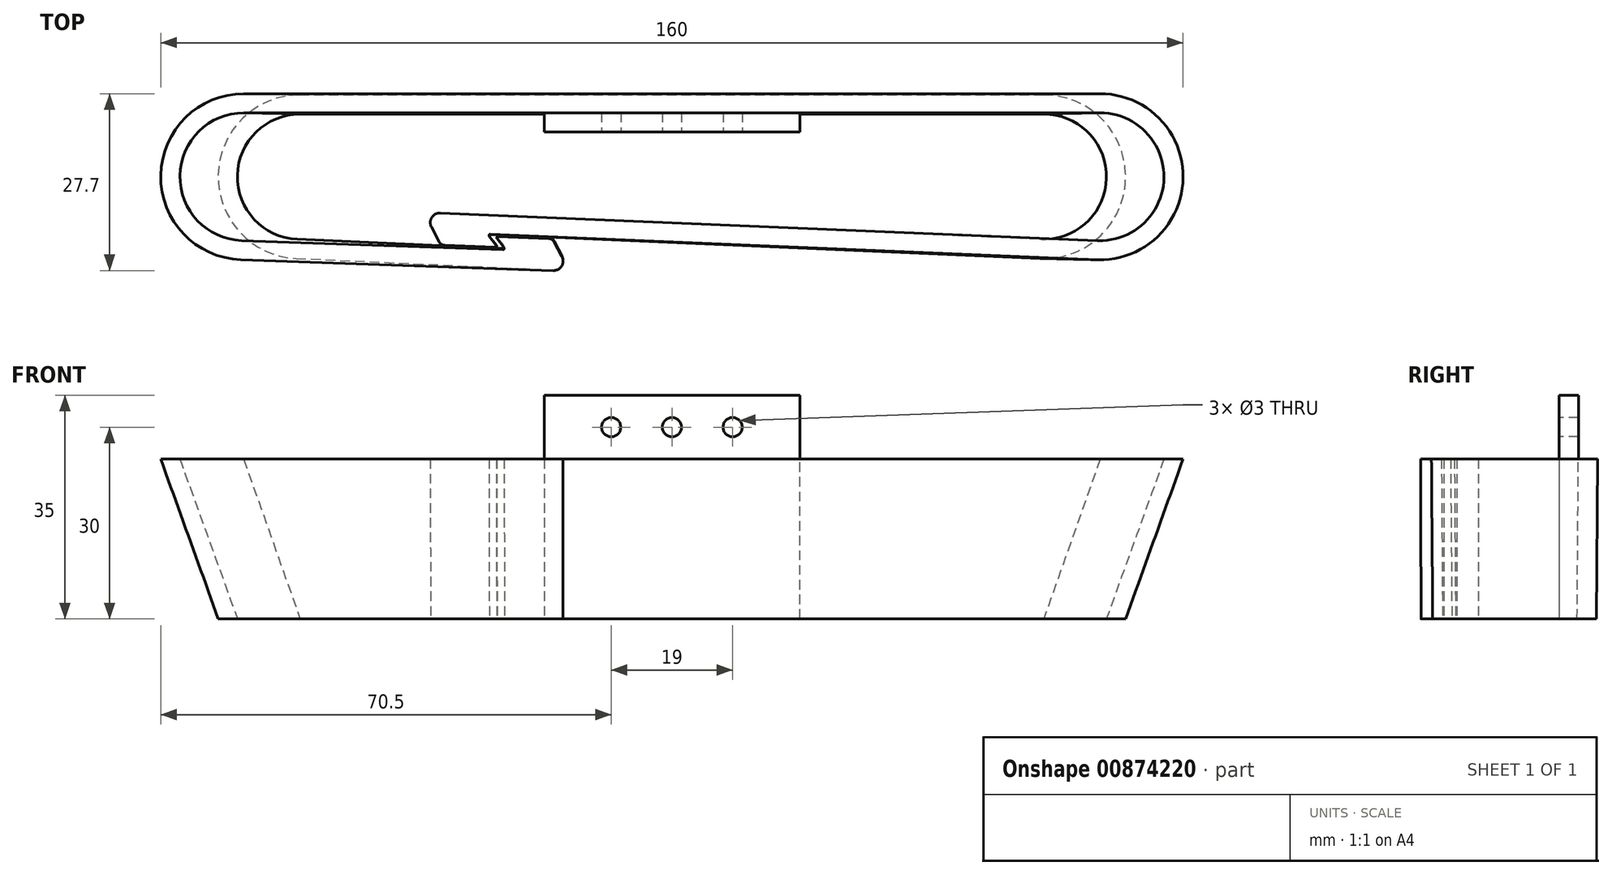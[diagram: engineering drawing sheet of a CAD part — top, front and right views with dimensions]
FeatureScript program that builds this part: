
annotation { "Feature Type Name" : "Feature", "Feature Type Description" : "" }
export const myFeature = defineFeature(function(context is Context, id is Id, definition is map)
    precondition{}
    {
        {
            var Q0;
            Q0=qCreatedBy(makeId("Top.planeOp"),FACE);
            var sketch = newSketch(context, id + "F0", { "sketchPlane" : qUnion([Q0])});
            skPoint(sketch, "E0.middle", {"position": v(0, 0) * mm});
            skArc(sketch, "E1", {"start": v(66.46, -12.99) * mm, "mid": v(80, -0.27) * mm, "end": v(67, 13) * mm});
            skLineSegment(sketch, "E2", {"start": v(67, 13) * mm, "end": v(-67, 13) * mm});
            skArc(sketch, "E3", {"start": v(-67, 13) * mm, "mid": v(-80, 0.23) * mm, "end": v(-67.45, -13) * mm});
            skLineSegment(sketch, "E4", {"start": v(66.46, -12.99) * mm, "end": v(-28.42, -9.01) * mm});
            skLineSegment(sketch, "E5", {"start": v(0, 13) * mm, "end": v(0, -10.2) * mm, "construction": true});
            skLineSegment(sketch, "E6", {"start": v(-16, 0) * mm, "end": v(-16, -14.79) * mm, "construction": true});
            skLineSegment(sketch, "E7", {"start": v(-67.45, -13) * mm, "end": v(-18.6, -14.7) * mm});
            skLineSegment(sketch, "E8", {"start": v(-67, 0) * mm, "end": v(-16, 0) * mm, "construction": true});
            skLineSegment(sketch, "E9.0", {"start": v(66.58, -10) * mm, "end": v(-36.26, -5.68) * mm});
            skLineSegment(sketch, "E9.1", {"start": v(-67.35, -10) * mm, "end": v(-26.46, -11.42) * mm});
            skArc(sketch, "E9.2", {"start": v(-67, 10) * mm, "mid": v(-77, 0.17) * mm, "end": v(-67.35, -10) * mm});
            skLineSegment(sketch, "E9.3", {"start": v(67, 10) * mm, "end": v(-67, 10) * mm});
            skArc(sketch, "E9.4", {"start": v(66.58, -10) * mm, "mid": v(77, -0.2) * mm, "end": v(67, 10) * mm});
            skLineSegment(sketch, "E10", {"start": v(-27.2, -9.4) * mm, "end": v(-19.29, -9.67) * mm});
            skLineSegment(sketch, "E11", {"start": v(-18.44, -10.2) * mm, "end": v(-17.22, -12.5) * mm});
            skPoint(sketch, "E12.visualSharp", {"position": v(-16, -14.79) * mm});
            skArc(sketch, "E12.filletArc", {"start": v(-18.6, -14.7) * mm, "mid": v(-17.27, -14) * mm, "end": v(-17.22, -12.5) * mm});
            skPoint(sketch, "E13.visualSharp", {"position": v(-18.71, -9.7) * mm});
            skArc(sketch, "E13.filletArc", {"start": v(-18.44, -10.2) * mm, "mid": v(-18.8, -9.82) * mm, "end": v(-19.29, -9.67) * mm});
            skPoint(sketch, "E14.visualSharp", {"position": v(-27.2, -9.4) * mm});
            skArc(sketch, "E14.filletArc", {"start": v(-27.2, -9.4) * mm, "mid": v(-27.4, -9.5) * mm, "end": v(-27.37, -9.72) * mm});
            skLineSegment(sketch, "E15", {"start": v(0, 0) * mm, "end": v(67, 0) * mm, "construction": true});
            skLineSegment(sketch, "E16", {"start": v(-28.59, -9.33) * mm, "end": v(-27.52, -10.72) * mm});
            skLineSegment(sketch, "E17", {"start": v(-27.69, -11.04) * mm, "end": v(-35.6, -10.71) * mm});
            skLineSegment(sketch, "E18", {"start": v(-36.45, -10.18) * mm, "end": v(-37.65, -7.87) * mm});
            skPoint(sketch, "E19.visualSharp", {"position": v(-36.18, -10.69) * mm});
            skArc(sketch, "E19.filletArc", {"start": v(-36.45, -10.18) * mm, "mid": v(-36.1, -10.56) * mm, "end": v(-35.6, -10.71) * mm});
            skPoint(sketch, "E20.visualSharp", {"position": v(-38.85, -5.57) * mm});
            skArc(sketch, "E20.filletArc", {"start": v(-36.26, -5.68) * mm, "mid": v(-37.59, -6.38) * mm, "end": v(-37.65, -7.87) * mm});
            skArc(sketch, "E21.filletArc", {"start": v(-27.69, -11.04) * mm, "mid": v(-27.5, -10.94) * mm, "end": v(-27.52, -10.72) * mm});
            skPoint(sketch, "E22.visualSharp", {"position": v(-28.85, -9) * mm});
            skArc(sketch, "E22.filletArc", {"start": v(-28.42, -9.01) * mm, "mid": v(-28.6, -9.12) * mm, "end": v(-28.59, -9.33) * mm});
            skLineSegment(sketch, "E23", {"start": v(-16, 0) * mm, "end": v(0, 0) * mm, "construction": true});
            skArc(sketch, "E24", {"start": v(-26.46, -11.42) * mm, "mid": v(-26.27, -11.31) * mm, "end": v(-26.3, -11.1) * mm});
            skLineSegment(sketch, "E25", {"start": v(-27.37, -9.72) * mm, "end": v(-26.3, -11.1) * mm});
            skLineSegment(sketch, "E26", {"start": v(-27.37, -9.47) * mm, "end": v(-27.37, -10.97) * mm, "construction": true});
            skLineSegment(sketch, "E27", {"start": v(-27.52, -10.72) * mm, "end": v(-27.52, -9.22) * mm, "construction": true});
            skSolve(sketch);
        }
        {
            var Q0;
            Q0=qCreatedBy(makeId("Top.planeOp"),FACE);
            cPlane(context, id + "F1", {"entities" : qUnion([Q0]), "cplaneType" : CPlaneType.OFFSET, "offset" : 25 * mm, "oppositeDirection" : true, "width" : 150 * mm, "height" : 150 * mm});
        }
        {
            var Q0;
            Q0=qCreatedBy(id+"F1.planeOp",FACE);
            var sketch = newSketch(context, id + "F2", { "sketchPlane" : qUnion([Q0])});
            skPoint(sketch, "E28.middle", {"position": v(0, 0) * mm});
            skArc(sketch, "E29", {"start": v(57.64, -12.79) * mm, "mid": v(71, -0.28) * mm, "end": v(58.2, 12.8) * mm});
            skLineSegment(sketch, "E30", {"start": v(58.2, 12.8) * mm, "end": v(-58.2, 12.8) * mm});
            skArc(sketch, "E31", {"start": v(-58.2, 12.8) * mm, "mid": v(-71, 0.3) * mm, "end": v(-58.78, -12.79) * mm});
            skLineSegment(sketch, "E32", {"start": v(57.64, -12.79) * mm, "end": v(-28.37, -9.03) * mm});
            skLineSegment(sketch, "E33", {"start": v(0, 12.8) * mm, "end": v(0, -10.27) * mm, "construction": true});
            skLineSegment(sketch, "E34", {"start": v(-16, 0) * mm, "end": v(-16, -14.73) * mm, "construction": true});
            skLineSegment(sketch, "E35", {"start": v(-58.78, -12.79) * mm, "end": v(-18.6, -14.61) * mm});
            skLineSegment(sketch, "E36", {"start": v(-58.2, 0) * mm, "end": v(-16, 0) * mm, "construction": true});
            skLineSegment(sketch, "E37.0", {"start": v(57.77, -9.8) * mm, "end": v(-36.2, -5.69) * mm});
            skLineSegment(sketch, "E37.1", {"start": v(-58.64, -9.79) * mm, "end": v(-26.42, -11.25) * mm});
            skArc(sketch, "E37.2", {"start": v(-58.2, 9.8) * mm, "mid": v(-68, 0.22) * mm, "end": v(-58.64, -9.79) * mm});
            skLineSegment(sketch, "E37.3", {"start": v(58.2, 9.8) * mm, "end": v(-58.2, 9.8) * mm});
            skArc(sketch, "E37.4", {"start": v(57.77, -9.8) * mm, "mid": v(68, -0.21) * mm, "end": v(58.2, 9.8) * mm});
            skLineSegment(sketch, "E38", {"start": v(-27.15, -9.22) * mm, "end": v(-19.23, -9.58) * mm});
            skLineSegment(sketch, "E39", {"start": v(-18.4, -10.12) * mm, "end": v(-17.2, -12.42) * mm});
            skPoint(sketch, "E40.visualSharp", {"position": v(-16, -14.73) * mm});
            skArc(sketch, "E40.filletArc", {"start": v(-18.6, -14.61) * mm, "mid": v(-17.26, -13.92) * mm, "end": v(-17.2, -12.42) * mm});
            skPoint(sketch, "E41.visualSharp", {"position": v(-18.66, -9.6) * mm});
            skArc(sketch, "E41.filletArc", {"start": v(-18.4, -10.12) * mm, "mid": v(-18.74, -9.73) * mm, "end": v(-19.23, -9.58) * mm});
            skPoint(sketch, "E42.visualSharp", {"position": v(-27.15, -9.22) * mm});
            skArc(sketch, "E42.filletArc", {"start": v(-27.15, -9.22) * mm, "mid": v(-27.33, -9.33) * mm, "end": v(-27.32, -9.54) * mm});
            skLineSegment(sketch, "E43", {"start": v(0, 0) * mm, "end": v(58.2, 0) * mm, "construction": true});
            skLineSegment(sketch, "E44", {"start": v(-28.53, -9.35) * mm, "end": v(-27.47, -10.74) * mm});
            skLineSegment(sketch, "E45", {"start": v(-27.63, -11.07) * mm, "end": v(-35.55, -10.72) * mm});
            skLineSegment(sketch, "E46", {"start": v(-36.4, -10.18) * mm, "end": v(-37.6, -7.88) * mm});
            skPoint(sketch, "E47.visualSharp", {"position": v(-36.13, -10.7) * mm});
            skArc(sketch, "E47.filletArc", {"start": v(-36.4, -10.18) * mm, "mid": v(-36.04, -10.57) * mm, "end": v(-35.55, -10.72) * mm});
            skPoint(sketch, "E48.visualSharp", {"position": v(-38.8, -5.57) * mm});
            skArc(sketch, "E48.filletArc", {"start": v(-36.2, -5.69) * mm, "mid": v(-37.53, -6.38) * mm, "end": v(-37.6, -7.88) * mm});
            skArc(sketch, "E49.filletArc", {"start": v(-27.63, -11.07) * mm, "mid": v(-27.45, -10.96) * mm, "end": v(-27.47, -10.74) * mm});
            skPoint(sketch, "E50.visualSharp", {"position": v(-28.8, -9.01) * mm});
            skArc(sketch, "E50.filletArc", {"start": v(-28.37, -9.03) * mm, "mid": v(-28.55, -9.14) * mm, "end": v(-28.53, -9.35) * mm});
            skLineSegment(sketch, "E51", {"start": v(-16, 0) * mm, "end": v(0, 0) * mm, "construction": true});
            skArc(sketch, "E52", {"start": v(-26.42, -11.25) * mm, "mid": v(-26.23, -11.15) * mm, "end": v(-26.25, -10.93) * mm});
            skLineSegment(sketch, "E53", {"start": v(-27.32, -9.54) * mm, "end": v(-26.25, -10.93) * mm});
            skLineSegment(sketch, "E54", {"start": v(-27.32, -9.3) * mm, "end": v(-27.32, -10.8) * mm, "construction": true});
            skLineSegment(sketch, "E55", {"start": v(-27.47, -10.74) * mm, "end": v(-27.47, -9.24) * mm, "construction": true});
            skSolve(sketch);
        }
        {
            var Q0;
            Q0=qCreatedBy(makeId("Top.planeOp"),FACE);
            var sketch = newSketch(context, id + "F3", { "sketchPlane" : qUnion([Q0])});
            skLineSegment(sketch, "E56", {"start": v(20, 10) * mm, "end": v(20, 7) * mm});
            skLineSegment(sketch, "E57", {"start": v(20, 7) * mm, "end": v(-20, 7) * mm});
            skLineSegment(sketch, "E58", {"start": v(-20, 7) * mm, "end": v(-20, 10) * mm});
            skLineSegment(sketch, "E59", {"start": v(-20, 10) * mm, "end": v(20, 10) * mm});
            skPoint(sketch, "E60.visualSharp", {"position": v(-20, 7) * mm});
            skPoint(sketch, "E61.visualSharp", {"position": v(20, 7) * mm});
            skLineSegment(sketch, "E62", {"start": v(0, 7) * mm, "end": v(0, 10) * mm, "construction": true});
            skPoint(sketch, "E62.endSnap0", {"position": v(0, 10) * mm});
            skSolve(sketch);
        }
        {
            var Q0;
            Q0=qSketchRegion(id+"F0",true);
            var Q1;
            Q1=qSketchRegion(id+"F2",true);
            loft(context, id + "F4", {"sheetProfilesArray" : [{ "sheetProfileEntities" : qUnion([Q0]) }, { "sheetProfileEntities" : qUnion([Q1]) }]});
        }
        {
            var Q0;
            Q0=qSketchRegion(id+"F3",true);
            extrude(context, id + "F5", {"entities" : qUnion([Q0]), "operationType" : NewBodyOperationType.ADD, "depth" : 10 * mm, "offsetDistance" : 25 * mm, "hasSecondDirection" : true, "secondDirectionOppositeDirection" : true, "secondDirectionDepth" : 25 * mm});
        }
        {
            var Q0;
            Q0=makeQuery(id+"F5.opExtrude","SWEPT_FACE",FACE,{"disambiguationData":[OSD([sQuery(id+"F3.wireOp",EDGE,"E57")])]});
            var sketch = newSketch(context, id + "F6", { "sketchPlane" : qUnion([Q0])});
            skLineSegment(sketch, "E63", {"start": v(0, 10) * mm, "end": v(0, 5) * mm, "construction": true});
            skCircle(sketch, "E64", {"center": v(0, 5) * mm, "radius": 1.5 * mm});
            skCircle(sketch, "E65", {"center": v(9.5, 5) * mm, "radius": 1.5 * mm});
            skCircle(sketch, "E66", {"center": v(-9.5, 5) * mm, "radius": 1.5 * mm});
            skSolve(sketch);
        }
        {
            var Q0;
            Q0 = qSketchRegion(id + "F6", true);
            extrude(context, id + "F7", {"entities" : qUnion([Q0]), "operationType" : NewBodyOperationType.REMOVE, "endBound" : BoundingType.THROUGH_ALL, "oppositeDirection" : true, "depth" : 25 * mm, "offsetDistance" : 25 * mm});
        }
    });
